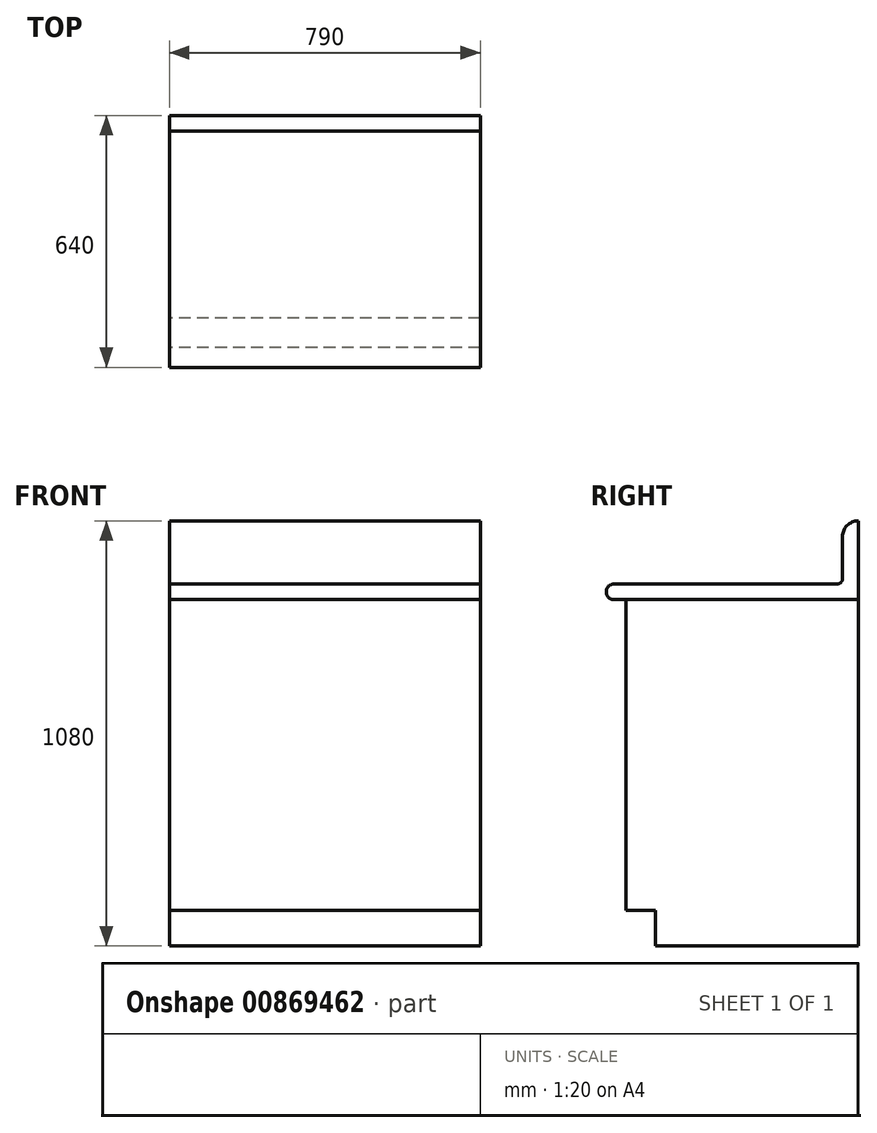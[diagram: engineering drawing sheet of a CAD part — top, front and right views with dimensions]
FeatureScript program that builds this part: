
annotation { "Feature Type Name" : "Feature", "Feature Type Description" : "" }
export const myFeature = defineFeature(function(context is Context, id is Id, definition is map)
    precondition{}
    {
        {
            var Q0;
            Q0=qCreatedBy(makeId("Top.planeOp"),FACE);
            var sketch = newSketch(context, id + "F0", { "sketchPlane" : qUnion([Q0])});
            skLineSegment(sketch, "E0.bottom", {"start": v(0, 0) * mm, "end": v(790, 0) * mm});
            skLineSegment(sketch, "E0.top", {"start": v(0, 590) * mm, "end": v(790, 590) * mm});
            skLineSegment(sketch, "E0.left", {"start": v(0, 0) * mm, "end": v(0, 590) * mm});
            skLineSegment(sketch, "E0.right", {"start": v(790, 0) * mm, "end": v(790, 590) * mm});
            skSolve(sketch);
        }
        {
            var Q0;
            Q0 = qSketchRegion(id + "F0", true);
            extrude(context, id + "F1", {"entities" : qUnion([Q0]), "depth" : 880 * mm, "offsetDistance" : 25 * mm});
        }
        {
            var Q0;
            Q0=qCreatedBy(makeId("Right.planeOp"),FACE);
            var sketch = newSketch(context, id + "F2", { "sketchPlane" : qUnion([Q0])});
            skLineSegment(sketch, "E1.bottom", {"start": v(0, 0) * mm, "end": v(75, 0) * mm});
            skLineSegment(sketch, "E1.top", {"start": v(0, 90) * mm, "end": v(75, 90) * mm});
            skLineSegment(sketch, "E1.left", {"start": v(0, 0) * mm, "end": v(0, 90) * mm});
            skLineSegment(sketch, "E1.right", {"start": v(75, 0) * mm, "end": v(75, 90) * mm});
            skSolve(sketch);
        }
        {
            var Q0;
            Q0 = qSketchRegion(id + "F2", true);
            extrude(context, id + "F3", {"entities" : qUnion([Q0]), "operationType" : NewBodyOperationType.REMOVE, "endBound" : BoundingType.THROUGH_ALL, "depth" : 25 * mm, "offsetDistance" : 25 * mm});
        }
        {
            var Q0;
            Q0=qCreatedBy(makeId("Right.planeOp"),FACE);
            var sketch = newSketch(context, id + "F4", { "sketchPlane" : qUnion([Q0])});
            skLineSegment(sketch, "E2.0", {"start": v(0, 880) * mm, "end": v(590, 880) * mm, "construction": true});
            skLineSegment(sketch, "E3.bottom", {"start": v(590, 880) * mm, "end": v(-30, 880) * mm});
            skLineSegment(sketch, "E3.top", {"start": v(537.3, 920) * mm, "end": v(-30, 920) * mm});
            skLineSegment(sketch, "E3.left", {"start": v(590, 880) * mm, "end": v(590, 1080) * mm});
            skLineSegment(sketch, "E3.right", {"start": v(-50, 880) * mm, "end": v(-50, 920) * mm, "construction": true});
            skArc(sketch, "E4", {"start": v(-30, 920) * mm, "mid": v(-50, 900) * mm, "end": v(-30, 880) * mm});
            skLineSegment(sketch, "E5", {"start": v(550, 932.7) * mm, "end": v(550, 1040) * mm});
            skLineSegment(sketch, "E6", {"start": v(590, 1080) * mm, "end": v(590, 1080) * mm});
            skPoint(sketch, "E7.visualSharp", {"position": v(550, 1080) * mm});
            skArc(sketch, "E7.filletArc", {"start": v(590, 1080) * mm, "mid": v(561.72, 1068.28) * mm, "end": v(550, 1040) * mm});
            skPoint(sketch, "E8.newPointA", {"position": v(590, 920) * mm});
            skArc(sketch, "E8.filletArc", {"start": v(537.3, 920) * mm, "mid": v(546.28, 923.72) * mm, "end": v(550, 932.7) * mm});
            skSolve(sketch);
        }
        {
            var Q0;
            Q0 = qSketchRegion(id + "F4", true);
            var Q1;
            Q1=makeQuery(id+"F1.opExtrude","SWEPT_FACE",FACE,{"disambiguationData":[OSD([sQuery(id+"F0.wireOp",EDGE,"E0.right")])]});
            extrude(context, id + "F5", {"entities" : qUnion([Q0]), "endBound" : BoundingType.UP_TO_SURFACE, "depth" : 25 * mm, "endBoundEntityFace" : qUnion([Q1]), "offsetDistance" : 25 * mm});
        }
    });
